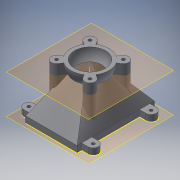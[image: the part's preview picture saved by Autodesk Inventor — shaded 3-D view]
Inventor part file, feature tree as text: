
AUTODESK INVENTOR PART (.ipt)
format: ipt  version: 2017 (Build 210142000, 142)  size: 525,824 bytes
history: native  units: mm
features: sketch x6, other x6, extrude x3, reference x3, projected_geometry x3, plane x2, loft x2, revolve x1, pattern_circular x1
ambient origin geometry x8: Origin, YZ Plane, XZ Plane, XY Plane, X Axis, Y Axis, Z Axis, Center Point
bodies: Solid1 (feature_tree)
feature tree (27):
  plane  "Work Plane1"
  extrude  "Extrusion1"  Depth=25.0mm
  plane  "Work Plane2"
  sketch  "Sketch2"  dims[d3=25.0mm d4=18.0mm]
  sketch  "Sketch3"  dims[d5=0.0mm d6=90.0deg d7=0.0mm d8=90.0deg]
  other  "Work Axis1"
  loft  "Loft1"
  loft  "Loft2"
  revolve  "Revolution1"  Angle=90.0deg
  extrude  "Extrusion2"  TaperAngle=90.0deg  [1 undecoded]
  pattern_circular  "Circular Pattern1"  [2 undecoded]
  extrude  "Extrusion3"  Depth=5.0mm
  sketch  "Sketch1"  dims[d0=5.0mm d1=0.0mm d2=25.0mm]
  reference  "Reference1"
  projected_geometry  "Projected Loop1"
  sketch  "Sketch4"  dims[d9=0.0mm d10=90.0deg d11=0.0mm d12=90.0deg]
  sketch  "Sketch5"  dims[d13=12.0mm d14=90.0deg]
  projected_geometry  "Projected Loop2"
  sketch  "Sketch6"  dims[d15=26.0mm d16=26.0mm d17=2.5mm d18=4.0mm d19=5.0mm d20=0.0mm d21=40.0mm d22=360.0deg d24=25.0mm d25=8.0mm d26=10.0mm d27=10.0mm d28=5.0mm d29=0.0mm]
  projected_geometry  "Projected Loop3"
  reference  "Reference2"
  reference  "Reference3"
  parser-record x1  (decoder bookkeeping rows leaked as tree rows — omitted from the tree; the rows remain in map.json)
  other  "gearbox.iam"
  other  "shifter box 1:1"
  other  "long selector:1"
  other  "short selector:1"
note: 3 required parameter values undecoded (feature->parameter linkage not recoverable at this tier; creation-order binding heuristic only, values carry confidence <= 0.55)
note: 1 file-system path scrubbed to <path> (originals preserved in map.json)
